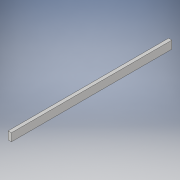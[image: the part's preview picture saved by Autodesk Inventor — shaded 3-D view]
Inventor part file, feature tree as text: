
AUTODESK INVENTOR PART (.ipt)
format: ipt  version: 2017 (Build 210142000, 142)  size: 91,648 bytes
history: native  units: in
note: dims shown in document units (in); Inventor stores cm internally (conversion verified against a paired STEP export)
features: extrude x1, sketch x1
ambient origin geometry x8: Origin, YZ Plane, XZ Plane, XY Plane, X Axis, Y Axis, Z Axis, Center Point
bodies: Solid1 (feature_tree)
feature tree (2):
  extrude  "Extrusion1"  Depth=72.0in
  sketch  "Sketch1"  dims[d0=1.5in d1=72.0in d2=3.5in d3=0.0in]
